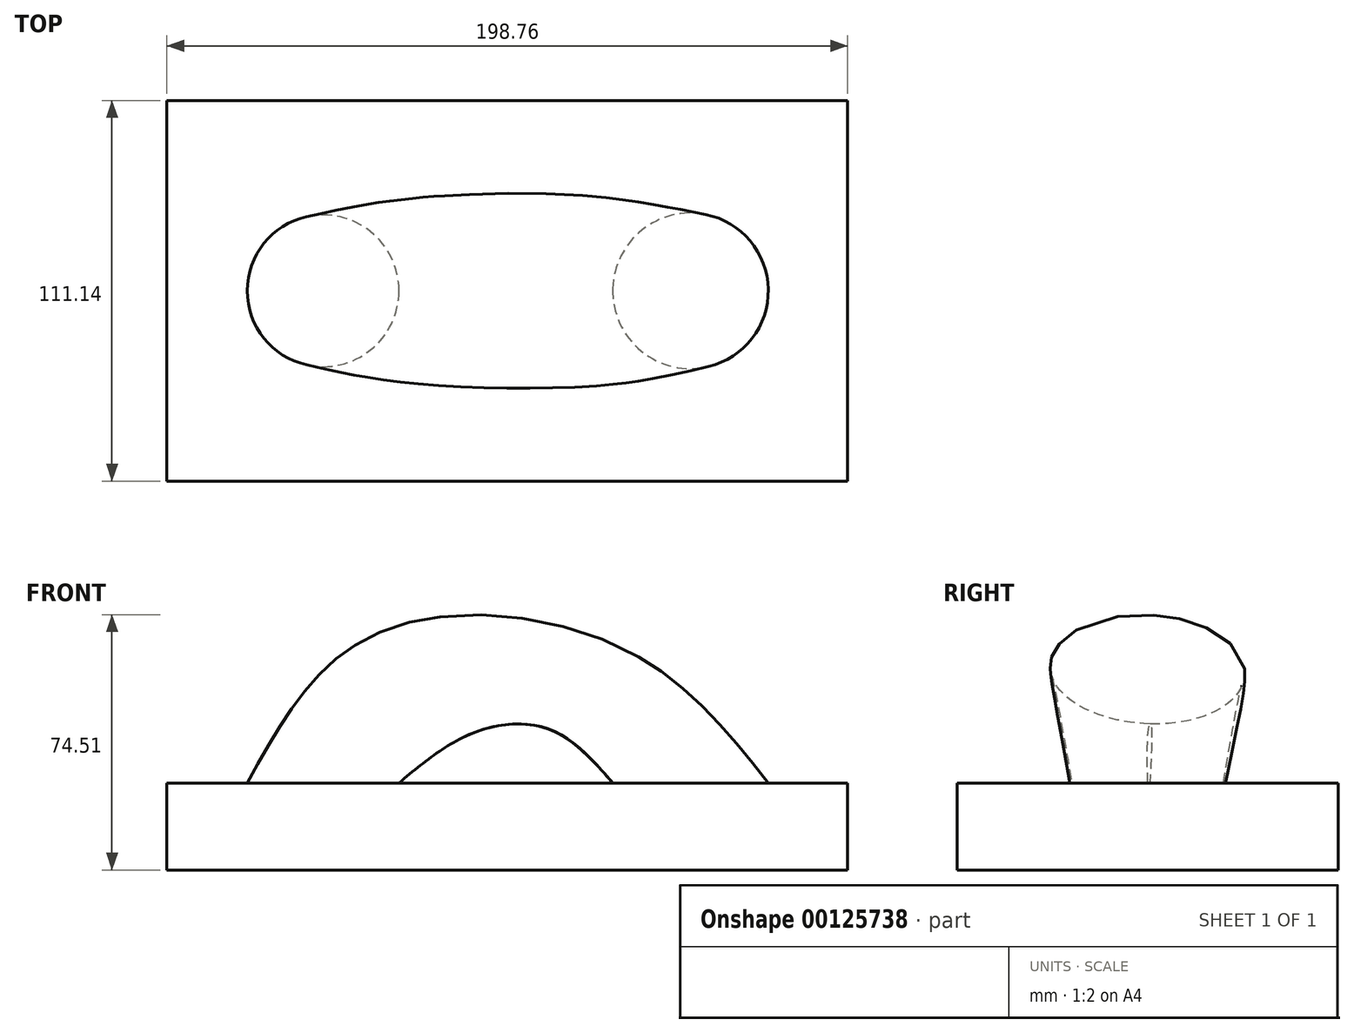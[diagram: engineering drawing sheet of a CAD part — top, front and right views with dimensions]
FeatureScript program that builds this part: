
annotation { "Feature Type Name" : "Feature", "Feature Type Description" : "" }
export const myFeature = defineFeature(function(context is Context, id is Id, definition is map)
    precondition{}
    {
        {
            var Q0;
            Q0=qCreatedBy(makeId("Top.planeOp"),FACE);
            var Q1;
            Q1=qCreatedBy(makeId("Right.planeOp"),FACE);
            cPlane(context, id + "F0", {"entities" : qUnion([Q0, Q1]), "cplaneType" : CPlaneType.MID_PLANE, "offset" : 25.4 * mm, "flipAlignment" : true, "width" : 152.4 * mm, "height" : 152.4 * mm});
        }
        {
            var Q0;
            Q0=qCreatedBy(makeId("Top.planeOp"),FACE);
            var sketch = newSketch(context, id + "F1", { "sketchPlane" : qUnion([Q0])});
            skCircle(sketch, "E0", {"center": v(-53.79, 0) * mm, "radius": 22.15 * mm});
            skCircle(sketch, "E1", {"center": v(53.49, 0) * mm, "radius": 22.7 * mm});
            skSolve(sketch);
        }
        {
            var Q0;
            Q0=qCreatedBy(id+"F0.planeOp",FACE);
            var sketch = newSketch(context, id + "F2", { "sketchPlane" : qUnion([Q0])});
            skEllipse(sketch, "E2", {"center": v(0, 38.89) * mm, "majorRadius": 26.97 * mm, "minorRadius": 20.27 * mm, "majorAxis": v(1, 0)});
            skSolve(sketch);
        }
        {
            var Q0;
            Q0=qCreatedBy(makeId("Top.planeOp"),FACE);
            var Q1;
            Q1=qCreatedBy(makeId("Right.planeOp"),FACE);
            cPlane(context, id + "F3", {"entities" : qUnion([Q0, Q1]), "cplaneType" : CPlaneType.MID_PLANE, "offset" : 25.4 * mm, "width" : 152.4 * mm, "height" : 152.4 * mm});
        }
        {
            var Q0;
            Q0=qCreatedBy(id+"F3.planeOp",FACE);
            var sketch = newSketch(context, id + "F4", { "sketchPlane" : qUnion([Q0])});
            skEllipse(sketch, "E3", {"center": v(0, 36.74) * mm, "majorRadius": 27.72 * mm, "minorRadius": 15.88 * mm, "majorAxis": v(1, 0.12)});
            skSolve(sketch);
        }
        {
            var Q0;
            Q0=makeQuery(id+"F1.imprint","IMPRINT",FACE,{"disambiguationData":[TD([[makeQuery(id+"F1.imprint","IMPRINT",EDGE,{"derivedFrom":sQuery(id+"F1.wireOp",EDGE,"E0")}),1.0]])]});
            var Q1;
            Q1=makeQuery(id+"F2.imprint","IMPRINT",FACE,{"disambiguationData":[TD([[makeQuery(id+"F2.imprint","IMPRINT",EDGE,{"derivedFrom":sQuery(id+"F2.wireOp",EDGE,"E2")}),1.0]])]});
            var Q2;
            Q2=makeQuery(id+"F4.imprint","IMPRINT",FACE,{"disambiguationData":[TD([[makeQuery(id+"F4.imprint","IMPRINT",EDGE,{"derivedFrom":sQuery(id+"F4.wireOp",EDGE,"E3")}),1.0]])]});
            var Q3;
            Q3=makeQuery(id+"F1.imprint","IMPRINT",FACE,{"disambiguationData":[TD([[makeQuery(id+"F1.imprint","IMPRINT",EDGE,{"derivedFrom":sQuery(id+"F1.wireOp",EDGE,"E1")}),1.0]])]});
            loft(context, id + "F5", {"sheetProfilesArray" : [{ "sheetProfileEntities" : qUnion([Q0]) }, { "sheetProfileEntities" : qUnion([Q1]) }, { "sheetProfileEntities" : qUnion([Q2]) }, { "sheetProfileEntities" : qUnion([Q3]) }]});
        }
        {
            var Q0;
            Q0=qCreatedBy(makeId("Top.planeOp"),FACE);
            var sketch = newSketch(context, id + "F6", { "sketchPlane" : qUnion([Q0])});
            skLineSegment(sketch, "E4.bottom", {"start": v(99.38, 55.57) * mm, "end": v(-99.38, 55.57) * mm});
            skLineSegment(sketch, "E4.top", {"start": v(99.38, -55.57) * mm, "end": v(-99.38, -55.57) * mm});
            skLineSegment(sketch, "E4.left", {"start": v(99.38, 55.57) * mm, "end": v(99.38, -55.57) * mm});
            skLineSegment(sketch, "E4.right", {"start": v(-99.38, 55.57) * mm, "end": v(-99.38, -55.57) * mm});
            skPoint(sketch, "E4.middle", {"position": v(0, 0) * mm});
            skSolve(sketch);
        }
        {
            var Q0;
            Q0=makeQuery(id+"F6.imprint","IMPRINT",FACE,{"disambiguationData":[TD([[makeQuery(id+"F6.imprint","IMPRINT",EDGE,{"derivedFrom":sQuery(id+"F6.wireOp",EDGE,"E4.bottom")}),1.0]])]});
            extrude(context, id + "F7", {"entities" : qUnion([Q0]), "operationType" : NewBodyOperationType.ADD, "oppositeDirection" : true, "depth" : 25.4 * mm});
        }
    });
